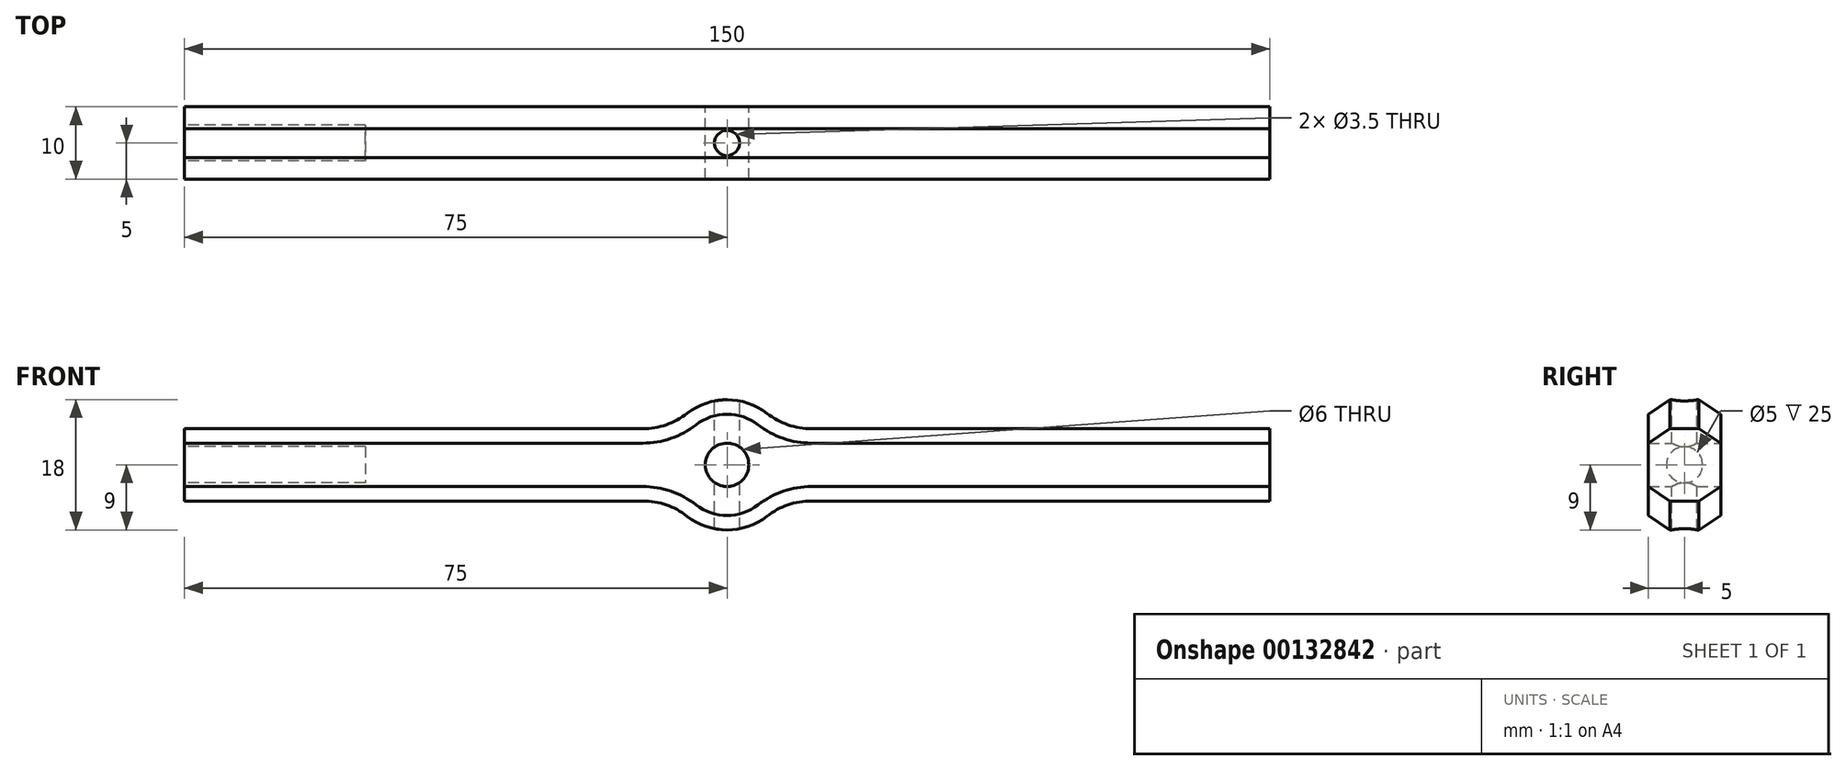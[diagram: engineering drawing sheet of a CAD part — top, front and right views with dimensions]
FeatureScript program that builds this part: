
annotation { "Feature Type Name" : "Feature", "Feature Type Description" : "" }
export const myFeature = defineFeature(function(context is Context, id is Id, definition is map)
    precondition{}
    {
        {
            var Q0;
            Q0=qCreatedBy(makeId("Front.planeOp"),FACE);
            var sketch = newSketch(context, id + "F0", { "sketchPlane" : qUnion([Q0])});
            skCircle(sketch, "E0", {"center": v(0, 0) * mm, "radius": 3 * mm});
            skLineSegment(sketch, "E1.bottom", {"start": v(7.48, 5) * mm, "end": v(75, 5) * mm});
            skLineSegment(sketch, "E1.top", {"start": v(7.48, -5) * mm, "end": v(75, -5) * mm});
            skLineSegment(sketch, "E1.left", {"start": v(7.48, 5) * mm, "end": v(7.48, -5) * mm, "construction": true});
            skLineSegment(sketch, "E1.right", {"start": v(75, 5) * mm, "end": v(75, -5) * mm});
            skLineSegment(sketch, "E2.bottom", {"start": v(-7.48, 5) * mm, "end": v(-75, 5) * mm});
            skLineSegment(sketch, "E2.top", {"start": v(-7.48, -5) * mm, "end": v(-75, -5) * mm});
            skLineSegment(sketch, "E2.left", {"start": v(-7.48, 5) * mm, "end": v(-7.48, -5) * mm, "construction": true});
            skLineSegment(sketch, "E2.right", {"start": v(-75, 5) * mm, "end": v(-75, -5) * mm});
            skLineSegment(sketch, "E3", {"start": v(-7.48, 5) * mm, "end": v(7.48, 5) * mm, "construction": true});
            skLineSegment(sketch, "E4", {"start": v(-7.48, -5) * mm, "end": v(7.48, -5) * mm, "construction": true});
            skArc(sketch, "E5", {"start": v(-7.48, 5) * mm, "mid": v(-9, 0) * mm, "end": v(-7.48, -5) * mm, "construction": true});
            skArc(sketch, "E6", {"start": v(-7.48, -5) * mm, "mid": v(0, -9) * mm, "end": v(7.48, -5) * mm});
            skArc(sketch, "E7", {"start": v(7.48, -5) * mm, "mid": v(9, 0) * mm, "end": v(7.48, 5) * mm, "construction": true});
            skArc(sketch, "E8", {"start": v(7.48, 5) * mm, "mid": v(0, 9) * mm, "end": v(-7.48, 5) * mm});
            skSolve(sketch);
        }
        {
            var Q0;
            Q0=qSketchRegion(id+"F0",true);
            extrude(context, id + "F1", {"entities" : qUnion([Q0]), "depth" : 10 * mm});
        }
        {
            var Q0;
            Q0=makeQuery(id+"F1.opExtrude","SWEPT_FACE",FACE,{"disambiguationData":[OSD([sQuery(id+"F0.wireOp",EDGE,"E2.right")])]});
            var sketch = newSketch(context, id + "F2", { "sketchPlane" : qUnion([Q0])});
            skCircle(sketch, "E9", {"center": v(5, 0) * mm, "radius": 2.5 * mm});
            skLineSegment(sketch, "E10", {"start": v(0, 5) * mm, "end": v(10, -5) * mm, "construction": true});
            skSolve(sketch);
        }
        {
            var Q0;
            Q0=qSketchRegion(id+"F2",true);
            extrude(context, id + "F3", {"entities" : qUnion([Q0]), "operationType" : NewBodyOperationType.REMOVE, "oppositeDirection" : true, "depth" : 25 * mm});
        }
        {
            var Q0;
            Q0=qCreatedBy(makeId("Top.planeOp"),FACE);
            var sketch = newSketch(context, id + "F4", { "sketchPlane" : qUnion([Q0])});
            skCircle(sketch, "E11", {"center": v(0, -5) * mm, "radius": 1.75 * mm});
            skSolve(sketch);
        }
        {
            var Q0;
            Q0=qSketchRegion(id+"F4",true);
            extrude(context, id + "F5", {"entities" : qUnion([Q0]), "operationType" : NewBodyOperationType.REMOVE, "endBound" : BoundingType.THROUGH_ALL, "oppositeDirection" : true, "depth" : 25 * mm, "hasSecondDirection" : true, "secondDirectionBound" : SecondDirectionBoundingType.THROUGH_ALL, "secondDirectionOppositeDirection" : false, "secondDirectionDepth" : 25 * mm});
        }
        {
            var Q0;
            Q0=makeQuery(id+"F1.opExtrude","SWEPT_EDGE",EDGE,{"disambiguationData":[OSD([sQuery(id+"F0.wireOp",EDGE,"E2.bottom"),sQuery(id+"F0.wireOp",EDGE,"E8")])]});
            var Q1;
            Q1=makeQuery(id+"F1.opExtrude","SWEPT_EDGE",EDGE,{"disambiguationData":[OSD([sQuery(id+"F0.wireOp",EDGE,"E1.bottom"),sQuery(id+"F0.wireOp",EDGE,"E8")])]});
            var Q2;
            Q2=makeQuery(id+"F1.opExtrude","SWEPT_EDGE",EDGE,{"disambiguationData":[OSD([sQuery(id+"F0.wireOp",EDGE,"E1.top"),sQuery(id+"F0.wireOp",EDGE,"E6")])]});
            var Q3;
            Q3=makeQuery(id+"F1.opExtrude","SWEPT_EDGE",EDGE,{"disambiguationData":[OSD([sQuery(id+"F0.wireOp",EDGE,"E2.top"),sQuery(id+"F0.wireOp",EDGE,"E6")])]});
            var Q4;
            Q4=makeQuery(id+"F8.boolean.opBoolean","INTERSECT",EDGE,{"derivedFrom":[makeQuery(id+"F1.opExtrude","SWEPT_FACE",FACE,{"disambiguationData":[OSD([sQuery(id+"F0.wireOp",EDGE,"E1.bottom")])]}),makeQuery(id+"F8.opExtrude","SWEPT_FACE",FACE,{"disambiguationData":[OSD([sQuery(id+"FqUPChPoVJXvrYf_1.wireOp",EDGE,"aNJPpA9v-C1Hh-cPNh-mDaa-UnRmCzPOYgnN")])]})]});
            var Q5;
            Q5=makeQuery(id+"F8.boolean.opBoolean","INTERSECT",EDGE,{"derivedFrom":[makeQuery(id+"F1.opExtrude","SWEPT_FACE",FACE,{"disambiguationData":[OSD([sQuery(id+"F0.wireOp",EDGE,"E2.bottom")])]}),makeQuery(id+"F8.opExtrude","SWEPT_FACE",FACE,{"disambiguationData":[OSD([sQuery(id+"FqUPChPoVJXvrYf_1.wireOp",EDGE,"aNJPpA9v-C1Hh-cPNh-mDaa-UnRmCzPOYgnN")])]})]});
            var Q6;
            Q6=makeQuery(id+"F8.boolean.opBoolean","INTERSECT",EDGE,{"derivedFrom":[makeQuery(id+"F1.opExtrude","SWEPT_FACE",FACE,{"disambiguationData":[OSD([sQuery(id+"F0.wireOp",EDGE,"E2.top")])]}),makeQuery(id+"F8.opExtrude","SWEPT_FACE",FACE,{"disambiguationData":[OSD([sQuery(id+"FqUPChPoVJXvrYf_1.wireOp",EDGE,"aNJPpA9v-C1Hh-cPNh-mDaa-UnRmCzPOYgnN")])]})]});
            var Q7;
            Q7=makeQuery(id+"F8.boolean.opBoolean","INTERSECT",EDGE,{"derivedFrom":[makeQuery(id+"F1.opExtrude","SWEPT_FACE",FACE,{"disambiguationData":[OSD([sQuery(id+"F0.wireOp",EDGE,"E1.top")])]}),makeQuery(id+"F8.opExtrude","SWEPT_FACE",FACE,{"disambiguationData":[OSD([sQuery(id+"FqUPChPoVJXvrYf_1.wireOp",EDGE,"aNJPpA9v-C1Hh-cPNh-mDaa-UnRmCzPOYgnN")])]})]});
            fillet(context, id + "F6", {"entities" : qUnion([Q0, Q1, Q2, Q3, Q4, Q5, Q6, Q7]), "radius" : 10 * mm, "tangentPropagation" : true, "allowEdgeOverflow" : false});
        }
        {
            var Q0;
            Q0=makeQuery(id+"F1.opExtrude","CAP_EDGE",EDGE,{"disambiguationData":[OSD([sQuery(id+"F0.wireOp",EDGE,"E2.bottom")])],"isStart":false});
            var Q1;
            Q1=makeQuery(id+"F1.opExtrude","CAP_EDGE",EDGE,{"disambiguationData":[OSD([sQuery(id+"F0.wireOp",EDGE,"E2.top")])],"isStart":false});
            var Q2;
            Q2=makeQuery(id+"F1.opExtrude","CAP_EDGE",EDGE,{"disambiguationData":[OSD([sQuery(id+"F0.wireOp",EDGE,"E2.bottom")])],"isStart":true});
            var Q3;
            Q3=makeQuery(id+"F1.opExtrude","CAP_EDGE",EDGE,{"disambiguationData":[OSD([sQuery(id+"F0.wireOp",EDGE,"E2.top")])],"isStart":true});
            chamfer(context, id + "F7", {"entities" : qUnion([Q0, Q1, Q2, Q3]), "chamferType" : ChamferType.TWO_OFFSETS, "width1" : 2 * mm, "oppositeDirection" : false, "width2" : 3 * mm, "tangentPropagation" : true});
        }
    });
